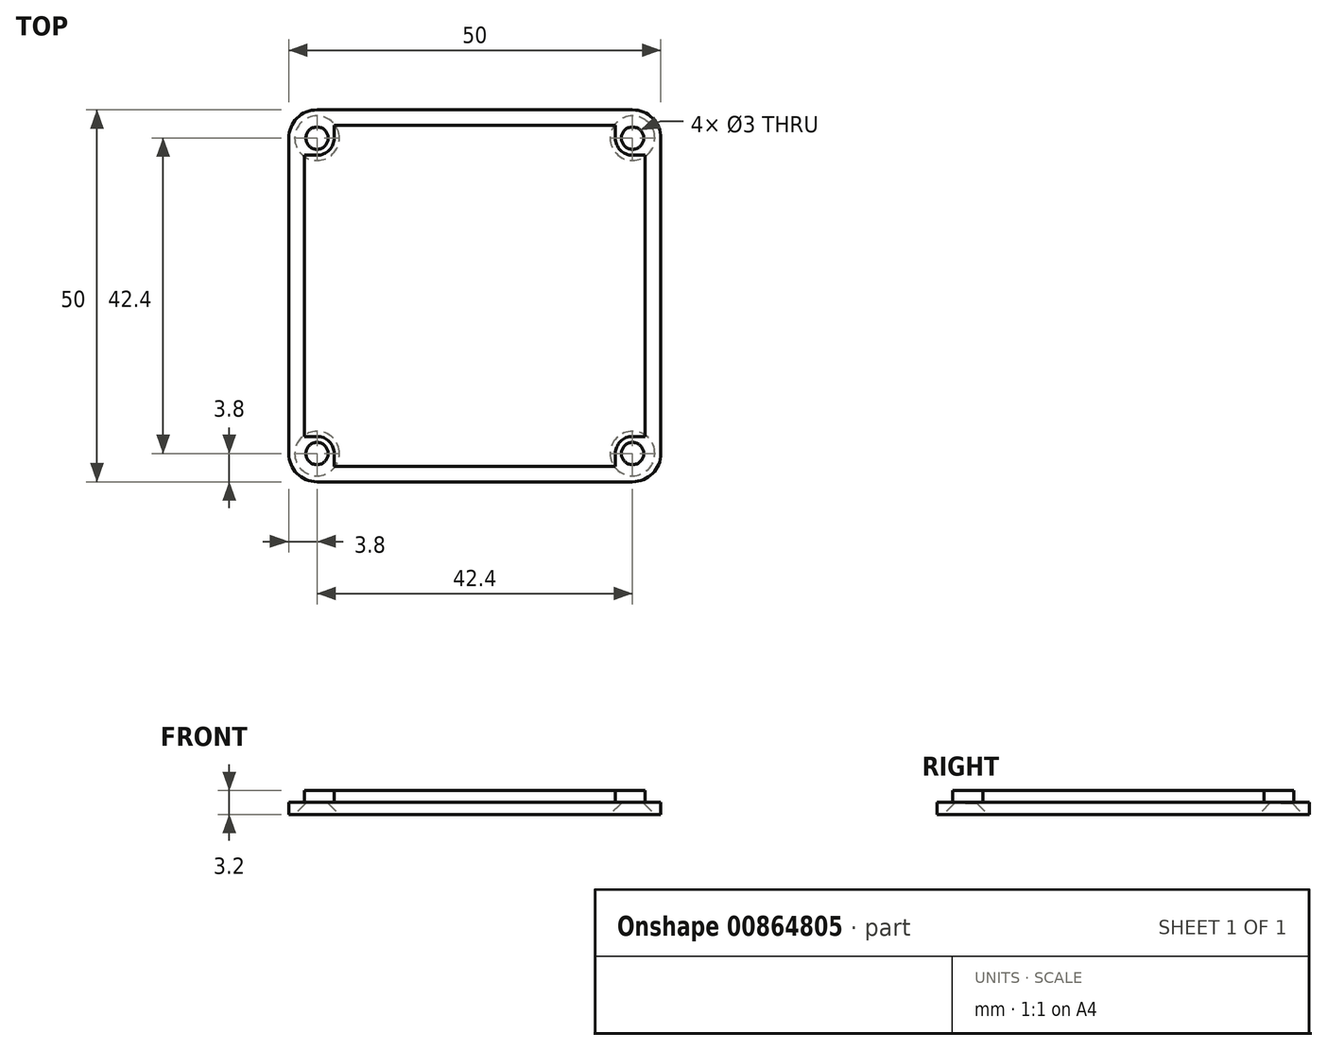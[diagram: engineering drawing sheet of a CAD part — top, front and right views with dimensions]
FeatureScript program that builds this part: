
annotation { "Feature Type Name" : "Feature", "Feature Type Description" : "" }
export const myFeature = defineFeature(function(context is Context, id is Id, definition is map)
    precondition{}
    {
        {
            assignVariable(context, id + "F0", {"name" : "thickness", "anyValue" : 1.6});
        }
        {
            var Q0;
            Q0=qCreatedBy(makeId("Top.planeOp"),FACE);
            var sketch = newSketch(context, id + "F1", { "sketchPlane" : qUnion([Q0])});
            skLineSegment(sketch, "E0", {"start": v(-25, 25) * mm, "end": v(25, 25) * mm, "construction": true});
            skLineSegment(sketch, "E1", {"start": v(-25, 25) * mm, "end": v(-25, -25) * mm, "construction": true});
            skLineSegment(sketch, "E2", {"start": v(-25, -25) * mm, "end": v(25, -25) * mm, "construction": true});
            skLineSegment(sketch, "E3", {"start": v(25, -25) * mm, "end": v(25, 25) * mm, "construction": true});
            skLineSegment(sketch, "E4", {"start": v(0, 25) * mm, "end": v(0, 0) * mm, "construction": true});
            skLineSegment(sketch, "E5", {"start": v(0, 0) * mm, "end": v(25, 0) * mm, "construction": true});
            skLineSegment(sketch, "E6", {"start": v(0, 0) * mm, "end": v(0, -25) * mm, "construction": true});
            skLineSegment(sketch, "E7", {"start": v(-25, 0) * mm, "end": v(0, 0) * mm, "construction": true});
            skLineSegment(sketch, "E8", {"start": v(-21.2, 25) * mm, "end": v(-21.2, -25) * mm, "construction": true});
            skLineSegment(sketch, "E9", {"start": v(-25, 21.2) * mm, "end": v(25, 21.2) * mm, "construction": true});
            skCircle(sketch, "E10", {"center": v(-21.2, 21.2) * mm, "radius": 1.5 * mm});
            skArc(sketch, "E11", {"start": v(-21.2, 25) * mm, "mid": v(-23.89, 23.89) * mm, "end": v(-25, 21.2) * mm});
            skLineSegment(sketch, "E12", {"start": v(-21.2, 25) * mm, "end": v(0, 25) * mm});
            skLineSegment(sketch, "E13", {"start": v(-25, 21.2) * mm, "end": v(-25, 0) * mm});
            skLineSegment(sketch, "E14", {"start": v(0, 22.9) * mm, "end": v(-18.9, 22.9) * mm});
            skLineSegment(sketch, "E15", {"start": v(-22.9, 18.9) * mm, "end": v(-22.9, 0) * mm});
            skArc(sketch, "E16", {"start": v(-21.2, 18.9) * mm, "mid": v(-19.57, 19.57) * mm, "end": v(-18.9, 21.2) * mm});
            skLineSegment(sketch, "E17", {"start": v(-18.9, 21.2) * mm, "end": v(-18.9, 22.9) * mm});
            skLineSegment(sketch, "E18", {"start": v(-21.2, 18.9) * mm, "end": v(-22.9, 18.9) * mm});
            skCircle(sketch, "E19.MirrorC", {"center": v(21.2, 21.2) * mm, "radius": 1.5 * mm});
            skArc(sketch, "E20.MirrorCS", {"start": v(21.2, 18.9) * mm, "mid": v(19.57, 19.57) * mm, "end": v(18.9, 21.2) * mm});
            skLineSegment(sketch, "E21.MirrorCS", {"start": v(21.2, 18.9) * mm, "end": v(22.9, 18.9) * mm});
            skLineSegment(sketch, "E22.MirrorCS", {"start": v(22.9, 18.9) * mm, "end": v(22.9, 0) * mm});
            skLineSegment(sketch, "E23.MirrorCS", {"start": v(18.9, 21.2) * mm, "end": v(18.9, 22.9) * mm});
            skLineSegment(sketch, "E24.MirrorCS", {"start": v(0, 22.9) * mm, "end": v(18.9, 22.9) * mm});
            skArc(sketch, "E25.MirrorCS", {"start": v(21.2, 25) * mm, "mid": v(23.89, 23.89) * mm, "end": v(25, 21.2) * mm});
            skLineSegment(sketch, "E26.MirrorCS", {"start": v(21.2, 25) * mm, "end": v(0, 25) * mm});
            skLineSegment(sketch, "E27.MirrorCS", {"start": v(25, 21.2) * mm, "end": v(25, 0) * mm});
            skLineSegment(sketch, "E28.MirrorCS", {"start": v(-25, -21.2) * mm, "end": v(-25, 0) * mm});
            skLineSegment(sketch, "E29.MirrorCS", {"start": v(-21.2, -25) * mm, "end": v(0, -25) * mm});
            skLineSegment(sketch, "E30.MirrorCS", {"start": v(25, -21.2) * mm, "end": v(25, 0) * mm});
            skLineSegment(sketch, "E31.MirrorCS", {"start": v(21.2, -25) * mm, "end": v(0, -25) * mm});
            skLineSegment(sketch, "E32.MirrorCS", {"start": v(21.2, -18.9) * mm, "end": v(22.9, -18.9) * mm});
            skCircle(sketch, "E33.MirrorC", {"center": v(21.2, -21.2) * mm, "radius": 1.5 * mm});
            skArc(sketch, "E34.MirrorCS", {"start": v(-21.2, -25) * mm, "mid": v(-23.89, -23.89) * mm, "end": v(-25, -21.2) * mm});
            skLineSegment(sketch, "E35.MirrorCS", {"start": v(-22.9, -18.9) * mm, "end": v(-22.9, 0) * mm});
            skLineSegment(sketch, "E36.MirrorCS", {"start": v(-18.9, -21.2) * mm, "end": v(-18.9, -22.9) * mm});
            skLineSegment(sketch, "E37.MirrorCS", {"start": v(-21.2, -18.9) * mm, "end": v(-22.9, -18.9) * mm});
            skLineSegment(sketch, "E38.MirrorCS", {"start": v(0, -22.9) * mm, "end": v(18.9, -22.9) * mm});
            skLineSegment(sketch, "E39.MirrorCS", {"start": v(18.9, -21.2) * mm, "end": v(18.9, -22.9) * mm});
            skArc(sketch, "E40.MirrorCS", {"start": v(21.2, -18.9) * mm, "mid": v(19.57, -19.57) * mm, "end": v(18.9, -21.2) * mm});
            skArc(sketch, "E41.MirrorCS", {"start": v(-21.2, -18.9) * mm, "mid": v(-19.57, -19.57) * mm, "end": v(-18.9, -21.2) * mm});
            skLineSegment(sketch, "E42.MirrorCS", {"start": v(22.9, -18.9) * mm, "end": v(22.9, 0) * mm});
            skLineSegment(sketch, "E43.MirrorCS", {"start": v(0, -22.9) * mm, "end": v(-18.9, -22.9) * mm});
            skArc(sketch, "E44.MirrorCS", {"start": v(21.2, -25) * mm, "mid": v(23.89, -23.89) * mm, "end": v(25, -21.2) * mm});
            skCircle(sketch, "E45.MirrorC", {"center": v(-21.2, -21.2) * mm, "radius": 1.5 * mm});
            skSolve(sketch);
        }
        {
            var Q0;
            Q0=makeQuery(id+"F1.imprint","IMPRINT",FACE,{"disambiguationData":[TD([[makeQuery(id+"F1.imprint","IMPRINT",EDGE,{"derivedFrom":sQuery(id+"F1.wireOp",EDGE,"E14")}),1.0]])]});
            extrude(context, id + "F2", {"entities" : qUnion([Q0]), "depth" : getVariable(context, 'thickness') * mm, "offsetDistance" : 25 * mm});
        }
        {
            var Q0;
            Q0=makeQuery(id+"F1.imprint","IMPRINT",FACE,{"disambiguationData":[TD([[makeQuery(id+"F1.imprint","IMPRINT",EDGE,{"derivedFrom":sQuery(id+"F1.wireOp",EDGE,"E10")}),-1.0]])]});
            var Q1;
            Q1=makeQuery(id+"F1.imprint","IMPRINT",FACE,{"disambiguationData":[TD([[makeQuery(id+"F1.imprint","IMPRINT",EDGE,{"derivedFrom":sQuery(id+"F1.wireOp",EDGE,"E14")}),1.0]])]});
            extrude(context, id + "F3", {"entities" : qUnion([Q0, Q1]), "operationType" : NewBodyOperationType.ADD, "oppositeDirection" : true, "depth" : (getVariable(context, 'thickness')) * mm, "offsetDistance" : 25 * mm});
        }
        {
            var Q0;
            Q0=makeQuery(id+"F3.opExtrude","CAP_FACE",FACE,{"disambiguationData":[OSD([sQuery(id+"F1.wireOp",EDGE,"E10"),sQuery(id+"F1.wireOp",EDGE,"E11"),sQuery(id+"F1.wireOp",EDGE,"E12"),sQuery(id+"F1.wireOp",EDGE,"E13"),sQuery(id+"F1.wireOp",EDGE,"E19.MirrorC"),sQuery(id+"F1.wireOp",EDGE,"E25.MirrorCS"),sQuery(id+"F1.wireOp",EDGE,"E26.MirrorCS"),sQuery(id+"F1.wireOp",EDGE,"E27.MirrorCS"),sQuery(id+"F1.wireOp",EDGE,"E28.MirrorCS"),sQuery(id+"F1.wireOp",EDGE,"E29.MirrorCS"),sQuery(id+"F1.wireOp",EDGE,"E30.MirrorCS"),sQuery(id+"F1.wireOp",EDGE,"E31.MirrorCS"),sQuery(id+"F1.wireOp",EDGE,"E33.MirrorC"),sQuery(id+"F1.wireOp",EDGE,"E34.MirrorCS"),sQuery(id+"F1.wireOp",EDGE,"E44.MirrorCS"),sQuery(id+"F1.wireOp",EDGE,"E45.MirrorC")])],"isStart":false});
            var sketch = newSketch(context, id + "F4", { "sketchPlane" : qUnion([Q0])});
            skCircle(sketch, "E46", {"center": v(-21.2, 21.2) * mm, "radius": 3 * mm});
            skCircle(sketch, "E47.MirrorC", {"center": v(21.2, 21.2) * mm, "radius": 3 * mm});
            skCircle(sketch, "E48.MirrorC", {"center": v(21.2, -21.2) * mm, "radius": 3 * mm});
            skCircle(sketch, "E49.MirrorC", {"center": v(-21.2, -21.2) * mm, "radius": 3 * mm});
            skSolve(sketch);
        }
        {
            var Q0;
            Q0 = qSketchRegion(id + "F4", true);
            extrude(context, id + "F5", {"entities" : qUnion([Q0]), "operationType" : NewBodyOperationType.REMOVE, "oppositeDirection" : true, "depth" : 25 * mm, "offsetDistance" : 25 * mm, "hasDraft" : true, "draftAngle" : 45 * degree, "draftPullDirection" : true});
        }
    });
